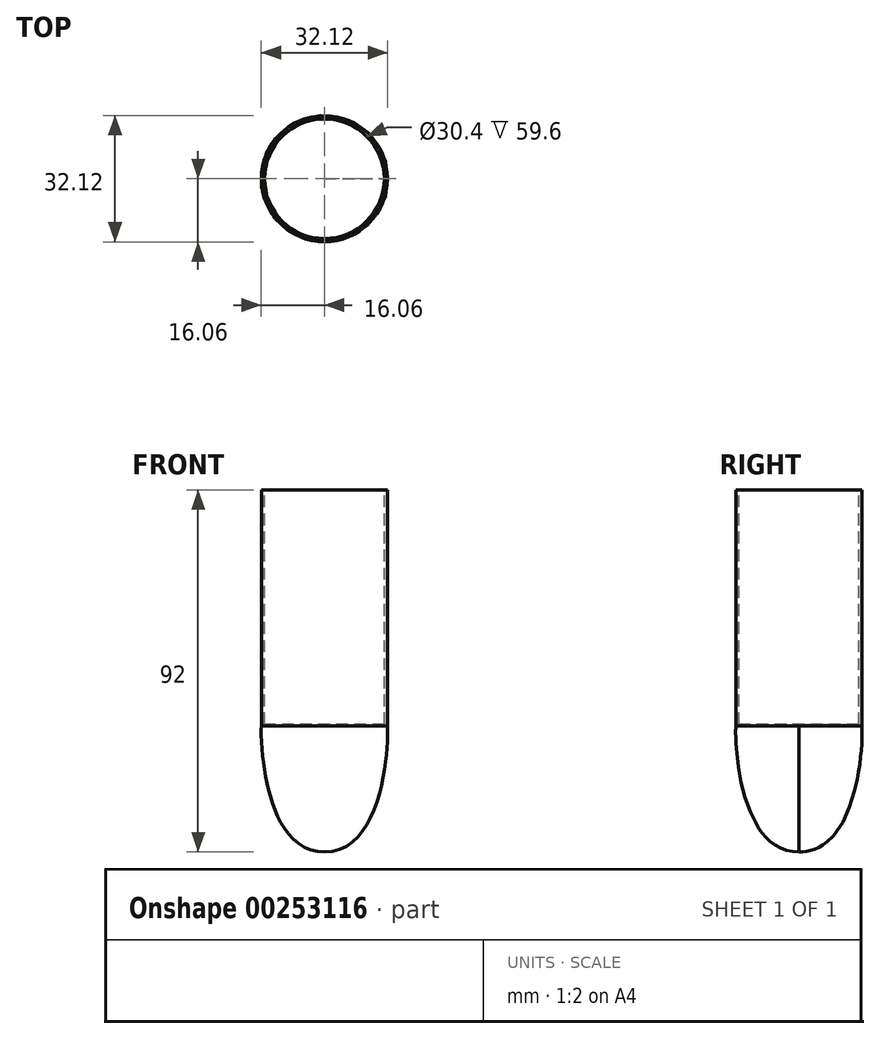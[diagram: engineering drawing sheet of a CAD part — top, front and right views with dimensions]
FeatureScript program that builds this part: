
annotation { "Feature Type Name" : "Feature", "Feature Type Description" : "" }
export const myFeature = defineFeature(function(context is Context, id is Id, definition is map)
    precondition{}
    {
        {
            var Q0;
            Q0=qCreatedBy(makeId("Top.planeOp"),FACE);
            var sketch = newSketch(context, id + "F0", { "sketchPlane" : qUnion([Q0])});
            skCircle(sketch, "E0", {"center": v(0, 0) * mm, "radius": 16 * mm});
            skSolve(sketch);
        }
        {
            var Q0;
            Q0 = qSketchRegion(id + "F0", true);
            extrude(context, id + "F1", {"entities" : qUnion([Q0]), "depth" : 60 * mm});
        }
        {
            var Q0;
            Q0=makeQuery(id+"F1.opExtrude","CAP_FACE",FACE,{"disambiguationData":[OSD([sQuery(id+"F0.wireOp",EDGE,"E0")])],"isStart":false});
            var sketch = newSketch(context, id + "F2", { "sketchPlane" : qUnion([Q0])});
            skCircle(sketch, "E1.0", {"center": v(0, 0) * mm, "radius": 15.2 * mm});
            skSolve(sketch);
        }
        {
            var Q0;
            Q0 = qSketchRegion(id + "F2", true);
            extrude(context, id + "F3", {"entities" : qUnion([Q0]), "operationType" : NewBodyOperationType.REMOVE, "oppositeDirection" : true, "depth" : 59.6 * mm});
        }
        {
            var Q0;
            Q0=makeQuery(id+"F1.opExtrude","CAP_FACE",FACE,{"disambiguationData":[OSD([sQuery(id+"F0.wireOp",EDGE,"E0")])],"isStart":true});
            var sketch = newSketch(context, id + "F4", { "sketchPlane" : qUnion([Q0])});
            skCircle(sketch, "E2.0", {"center": v(0, 0) * mm, "radius": 16 * mm});
            skSolve(sketch);
        }
        {
            var Q0;
            Q0=qCreatedBy(makeId("Front.planeOp"),FACE);
            var sketch = newSketch(context, id + "F5", { "sketchPlane" : qUnion([Q0])});
            skLineSegment(sketch, "E3.0", {"start": v(16, 0) * mm, "end": v(-16, 0) * mm, "construction": true});
            skLineSegment(sketch, "E4", {"start": v(0, 0) * mm, "end": v(0, -32) * mm, "construction": true});
            skFitSpline(sketch, "E5", {"points": [v(0, -32) * mm, v(16, 0) * mm], "startDerivative": vector(48.87, 0) * mm, "endDerivative": vector(-0.87, 1.47) * mm});
            skLineSegment(sketch, "E6", {"start": v(0, -32) * mm, "end": v(16.3, -32) * mm, "construction": true});
            skLineSegment(sketch, "E7", {"start": v(16, 0) * mm, "end": v(16.3, -32) * mm, "construction": true});
            skLineSegment(sketch, "E8", {"start": v(16, 0) * mm, "end": v(0, 0) * mm});
            skLineSegment(sketch, "E9", {"start": v(0, -32) * mm, "end": v(0, 0) * mm});
            skSolve(sketch);
        }
        {
            var Q0;
            Q0=qCreatedBy(makeId("Right.planeOp"),FACE);
            var sketch = newSketch(context, id + "F6", { "sketchPlane" : qUnion([Q0])});
            skLineSegment(sketch, "E10", {"start": v(0, -32.12) * mm, "end": v(0, 70.58) * mm, "construction": true});
            skSolve(sketch);
        }
        {
            var Q0;
            Q0 = qSketchRegion(id + "F5", true);
            var Q1;
            Q1=sQuery(id+"F6.wireOp",EDGE,"E10");
            revolve(context, id + "F7", {"operationType" : NewBodyOperationType.ADD, "entities" : qUnion([Q0]), "axis" : qUnion([Q1]), "revolveType" : RevolveType.FULL});
        }
    });
